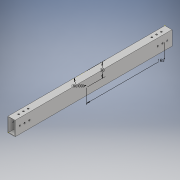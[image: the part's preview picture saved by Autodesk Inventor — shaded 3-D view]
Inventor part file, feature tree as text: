
AUTODESK INVENTOR PART (.ipt)
format: ipt  version: 2019 (Build 230136000, 136)  size: 174,080 bytes
history: native  units: mm
features: sketch x5, hole x2, other x1, extrude x1
ambient origin geometry x8: Origin, YZ Plane, XZ Plane, XY Plane, X Axis, Y Axis, Z Axis, Center Point
bodies: Body1 (feature_tree)
feature tree (9):
  other  "ソリッド1"
  extrude  "押し出し1"  Depth=15.0mm
  hole  "穴1"  [1 undecoded]
  hole  "穴2"  [1 undecoded]
  sketch  "スケッチ4"
  sketch  "スケッチ5"
  sketch  "スケッチ1"
  sketch  "スケッチ2"
  sketch  "スケッチ3"
note: 2 required parameter values undecoded (feature->parameter linkage not recoverable at this tier; creation-order binding heuristic only, values carry confidence <= 0.55)
